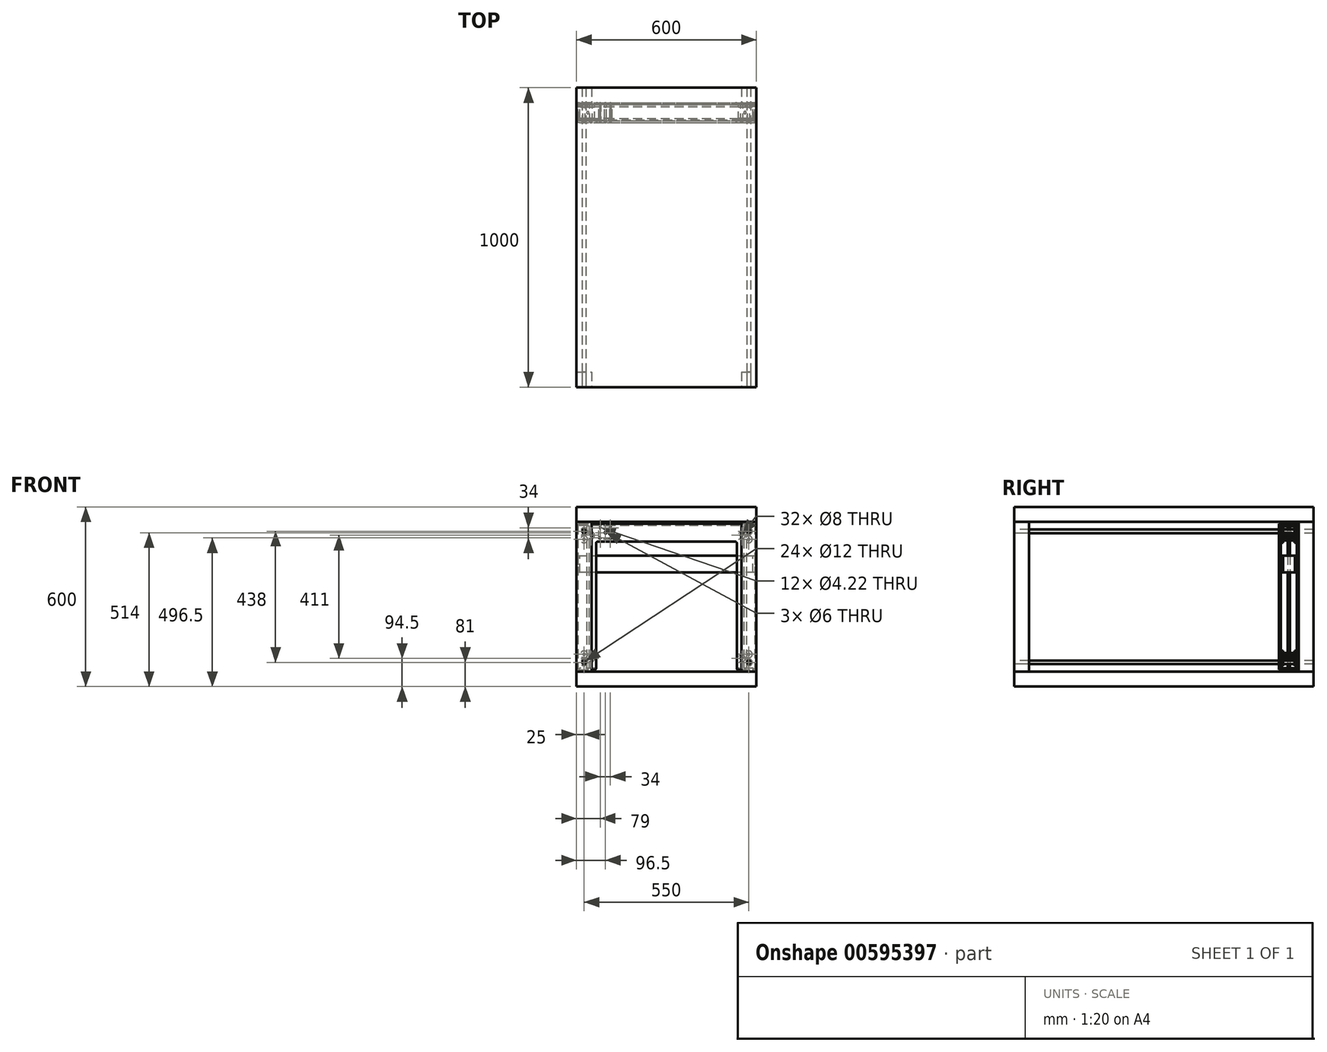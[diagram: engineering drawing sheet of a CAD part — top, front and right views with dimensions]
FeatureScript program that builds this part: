
annotation { "Feature Type Name" : "Feature", "Feature Type Description" : "" }
export const myFeature = defineFeature(function(context is Context, id is Id, definition is map)
    precondition{}
    {
        {
            var Q0;
            Q0=qCreatedBy(makeId("Front.planeOp"),FACE);
            var sketch = newSketch(context, id + "F0", { "sketchPlane" : qUnion([Q0])});
            skLineSegment(sketch, "E0.bottom", {"start": v(-300, 250) * mm, "end": v(-250, 250) * mm});
            skLineSegment(sketch, "E0.top", {"start": v(-300, -250) * mm, "end": v(-250, -250) * mm});
            skLineSegment(sketch, "E0.left", {"start": v(-300, 250) * mm, "end": v(-300, -250) * mm});
            skLineSegment(sketch, "E0.right", {"start": v(300, 250) * mm, "end": v(300, -250) * mm});
            skPoint(sketch, "E0.middle", {"position": v(0, 0) * mm});
            skLineSegment(sketch, "E1", {"start": v(-250, 250) * mm, "end": v(-250, -250) * mm});
            skLineSegment(sketch, "E2", {"start": v(-250, 250) * mm, "end": v(250, 250) * mm});
            skLineSegment(sketch, "E3", {"start": v(-250, -250) * mm, "end": v(250, -250) * mm});
            skLineSegment(sketch, "E4", {"start": v(250, -250) * mm, "end": v(250, 250) * mm});
            skLineSegment(sketch, "E5", {"start": v(250, 250) * mm, "end": v(300, 250) * mm});
            skLineSegment(sketch, "E6", {"start": v(250, -250) * mm, "end": v(300, -250) * mm});
            skLineSegment(sketch, "E7", {"start": v(-300, -250) * mm, "end": v(-300, -300) * mm});
            skLineSegment(sketch, "E8", {"start": v(-300, -300) * mm, "end": v(300, -300) * mm});
            skLineSegment(sketch, "E9", {"start": v(300, -300) * mm, "end": v(300, -250) * mm});
            skLineSegment(sketch, "E10", {"start": v(-300, 250) * mm, "end": v(-300, 300) * mm});
            skLineSegment(sketch, "E11", {"start": v(-300, 300) * mm, "end": v(300, 300) * mm});
            skLineSegment(sketch, "E12", {"start": v(300, 300) * mm, "end": v(300, 250) * mm});
            skLineSegment(sketch, "E13", {"start": v(-275, 250) * mm, "end": v(-275, 219) * mm, "construction": true});
            skLineSegment(sketch, "E14", {"start": v(275, -250) * mm, "end": v(275, 219) * mm, "construction": true});
            skCircle(sketch, "E15", {"center": v(-275, 219) * mm, "radius": 6 * mm});
            skCircle(sketch, "E16", {"center": v(275, 219) * mm, "radius": 6 * mm});
            skCircle(sketch, "E17", {"center": v(-275, -219) * mm, "radius": 6 * mm});
            skCircle(sketch, "E18", {"center": v(275, -219) * mm, "radius": 6 * mm});
            skLineSegment(sketch, "E19", {"start": v(-275, 219) * mm, "end": v(275, -219) * mm, "construction": true});
            skLineSegment(sketch, "E20", {"start": v(275, 219) * mm, "end": v(-275, -219) * mm, "construction": true});
            skLineSegment(sketch, "E21", {"start": v(275, 219) * mm, "end": v(275, 250) * mm, "construction": true});
            skLineSegment(sketch, "E22", {"start": v(-275, 219) * mm, "end": v(-275, -250) * mm, "construction": true});
            skSolve(sketch);
        }
        {
            var Q0;
            Q0=makeQuery(id+"F0.imprint","IMPRINT",FACE,{"disambiguationData":[TD([[makeQuery(id+"F0.imprint","IMPRINT",EDGE,{"derivedFrom":sQuery(id+"F0.wireOp",EDGE,"E0.bottom")}),1.0]])]});
            var Q1;
            Q1=makeQuery(id+"F0.imprint","IMPRINT",FACE,{"disambiguationData":[TD([[makeQuery(id+"F0.imprint","IMPRINT",EDGE,{"derivedFrom":sQuery(id+"F0.wireOp",EDGE,"E0.top")}),-1.0]])]});
            extrude(context, id + "F1", {"entities" : qUnion([Q0, Q1]), "oppositeDirection" : true, "depth" : 1000 * mm, "offsetDistance" : 25 * mm});
        }
        {
            var Q0;
            Q0=makeQuery(id+"F0.imprint","IMPRINT",FACE,{"disambiguationData":[TD([[makeQuery(id+"F0.imprint","IMPRINT",EDGE,{"derivedFrom":sQuery(id+"F0.wireOp",EDGE,"E0.bottom")}),-1.0]])]});
            var Q1;
            Q1=makeQuery(id+"F0.imprint","IMPRINT",FACE,{"disambiguationData":[TD([[makeQuery(id+"F0.imprint","IMPRINT",EDGE,{"derivedFrom":sQuery(id+"F0.wireOp",EDGE,"E0.right")}),-1.0]])]});
            extrude(context, id + "F2", {"entities" : qUnion([Q0, Q1]), "oppositeDirection" : true, "depth" : 50 * mm, "offsetDistance" : 25 * mm});
        }
        {
            var Q0;
            Q0=makeQuery(id+"F0.imprint","IMPRINT",FACE,{"disambiguationData":[TD([[makeQuery(id+"F0.imprint","IMPRINT",EDGE,{"derivedFrom":sQuery(id+"F0.wireOp",EDGE,"E0.bottom")}),-1.0]])]});
            var Q1;
            Q1=makeQuery(id+"F0.imprint","IMPRINT",FACE,{"disambiguationData":[TD([[makeQuery(id+"F0.imprint","IMPRINT",EDGE,{"derivedFrom":sQuery(id+"F0.wireOp",EDGE,"E0.right")}),-1.0]])]});
            var Q2;
            Q2=makeQuery(id+"F1.opExtrude","CAP_FACE",FACE,{"disambiguationData":[OSD([sQuery(id+"F0.wireOp",EDGE,"E0.bottom"),sQuery(id+"F0.wireOp",EDGE,"E2"),sQuery(id+"F0.wireOp",EDGE,"E5"),sQuery(id+"F0.wireOp",EDGE,"E10"),sQuery(id+"F0.wireOp",EDGE,"E11"),sQuery(id+"F0.wireOp",EDGE,"E12")])],"isStart":false});
            var Q3;
            Q3=makeQuery(id+"F1.opExtrude","CAP_FACE",FACE,{"disambiguationData":[OSD([sQuery(id+"F0.wireOp",EDGE,"E0.bottom"),sQuery(id+"F0.wireOp",EDGE,"E2"),sQuery(id+"F0.wireOp",EDGE,"E5"),sQuery(id+"F0.wireOp",EDGE,"E10"),sQuery(id+"F0.wireOp",EDGE,"E11"),sQuery(id+"F0.wireOp",EDGE,"E12")])],"isStart":false});
            extrude(context, id + "F3", {"entities" : qUnion([Q0, Q1]), "endBound" : BoundingType.UP_TO_SURFACE, "oppositeDirection" : true, "depth" : 1000 * mm, "endBoundEntityFace" : qUnion([Q2]), "offsetDistance" : 25 * mm, "hasSecondDirection" : true, "secondDirectionBound" : SecondDirectionBoundingType.UP_TO_SURFACE, "secondDirectionOppositeDirection" : true, "secondDirectionDepth" : 950 * mm, "secondDirectionBoundEntityFace" : qUnion([Q3]), "hasSecondDirectionOffset" : true, "secondDirectionOffsetDistance" : 50 * mm});
        }
        {
            var Q0;
            Q0=makeQuery(id+"F0.imprint","IMPRINT",FACE,{"disambiguationData":[TD([[makeQuery(id+"F0.imprint","IMPRINT",EDGE,{"derivedFrom":sQuery(id+"F0.wireOp",EDGE,"E15")}),1.0]])]});
            var Q1;
            Q1=makeQuery(id+"F0.imprint","IMPRINT",FACE,{"disambiguationData":[TD([[makeQuery(id+"F0.imprint","IMPRINT",EDGE,{"derivedFrom":sQuery(id+"F0.wireOp",EDGE,"E17")}),1.0]])]});
            var Q2;
            Q2=makeQuery(id+"F0.imprint","IMPRINT",FACE,{"disambiguationData":[TD([[makeQuery(id+"F0.imprint","IMPRINT",EDGE,{"derivedFrom":sQuery(id+"F0.wireOp",EDGE,"E18")}),1.0]])]});
            var Q3;
            Q3=makeQuery(id+"F0.imprint","IMPRINT",FACE,{"disambiguationData":[TD([[makeQuery(id+"F0.imprint","IMPRINT",EDGE,{"derivedFrom":sQuery(id+"F0.wireOp",EDGE,"E16")}),1.0]])]});
            var Q4;
            {Q4=qUnion([makeQuery(id+"F3.opExtrude","CAP_FACE",FACE,{"disambiguationData":[OSD([sQuery(id+"F0.wireOp",EDGE,"E0.bottom"),sQuery(id+"F0.wireOp",EDGE,"E0.top"),sQuery(id+"F0.wireOp",EDGE,"E0.left"),sQuery(id+"F0.wireOp",EDGE,"E1"),sQuery(id+"F0.wireOp",EDGE,"E15"),sQuery(id+"F0.wireOp",EDGE,"E17")])],"isStart":false}),makeQuery(id+"F3.opExtrude","CAP_FACE",FACE,{"disambiguationData":[OSD([sQuery(id+"F0.wireOp",EDGE,"E0.right"),sQuery(id+"F0.wireOp",EDGE,"E4"),sQuery(id+"F0.wireOp",EDGE,"E5"),sQuery(id+"F0.wireOp",EDGE,"E6"),sQuery(id+"F0.wireOp",EDGE,"E16"),sQuery(id+"F0.wireOp",EDGE,"E18")])],"isStart":false})]);}
            extrude(context, id + "F4", {"entities" : qUnion([Q0, Q1, Q2, Q3]), "endBound" : BoundingType.UP_TO_SURFACE, "oppositeDirection" : true, "depth" : 25 * mm, "endBoundEntityFace" : qUnion([Q4]), "offsetDistance" : 25 * mm});
        }
        {
            var Q0;
            Q0=makeQuery(id+"F3.opExtrude","CAP_FACE",FACE,{"disambiguationData":[OSD([sQuery(id+"F0.wireOp",EDGE,"E0.bottom"),sQuery(id+"F0.wireOp",EDGE,"E0.top"),sQuery(id+"F0.wireOp",EDGE,"E0.left"),sQuery(id+"F0.wireOp",EDGE,"E1"),sQuery(id+"F0.wireOp",EDGE,"E15"),sQuery(id+"F0.wireOp",EDGE,"E17")])],"isStart":true});
            var sketch = newSketch(context, id + "F5", { "sketchPlane" : qUnion([Q0])});
            skLineSegment(sketch, "E23.1.0", {"start": v(250, -250) * mm, "end": v(300, -250) * mm, "construction": true});
            skLineSegment(sketch, "E23.1.1", {"start": v(300, -250) * mm, "end": v(300, 250) * mm, "construction": true});
            skLineSegment(sketch, "E23.1.2", {"start": v(300, 250) * mm, "end": v(250, 250) * mm, "construction": true});
            skLineSegment(sketch, "E23.1.3", {"start": v(250, 250) * mm, "end": v(250, -250) * mm, "construction": true});
            skLineSegment(sketch, "E24.0.0", {"start": v(-300, 250) * mm, "end": v(-300, -250) * mm, "construction": true});
            skLineSegment(sketch, "E24.0.1", {"start": v(-300, -250) * mm, "end": v(-250, -250) * mm, "construction": true});
            skLineSegment(sketch, "E24.0.2", {"start": v(-250, -250) * mm, "end": v(-250, 250) * mm, "construction": true});
            skLineSegment(sketch, "E24.0.3", {"start": v(-250, 250) * mm, "end": v(-300, 250) * mm, "construction": true});
            skCircle(sketch, "E25.0", {"center": v(-275, 219) * mm, "radius": 6 * mm});
            skCircle(sketch, "E25.1", {"center": v(-275, -219) * mm, "radius": 6 * mm});
            skCircle(sketch, "E26.0", {"center": v(275, -219) * mm, "radius": 6 * mm});
            skCircle(sketch, "E26.1", {"center": v(275, 219) * mm, "radius": 6 * mm});
            skLineSegment(sketch, "E27.0.1", {"start": v(300, 250) * mm, "end": v(300, 300) * mm, "construction": true});
            skLineSegment(sketch, "E27.0.2", {"start": v(300, 300) * mm, "end": v(-300, 300) * mm, "construction": true});
            skLineSegment(sketch, "E27.0.3", {"start": v(-300, 300) * mm, "end": v(-300, 250) * mm, "construction": true});
            skLineSegment(sketch, "E28.0.1", {"start": v(-300, -250) * mm, "end": v(-300, -300) * mm, "construction": true});
            skLineSegment(sketch, "E28.0.2", {"start": v(-300, -300) * mm, "end": v(300, -300) * mm, "construction": true});
            skLineSegment(sketch, "E28.0.3", {"start": v(300, -300) * mm, "end": v(300, -250) * mm, "construction": true});
            skLineSegment(sketch, "E29", {"start": v(-250, 250) * mm, "end": v(250, 250) * mm, "construction": true});
            skLineSegment(sketch, "E30", {"start": v(-250, -250) * mm, "end": v(250, -250) * mm, "construction": true});
            skCircle(sketch, "E31", {"center": v(-275, 219) * mm, "radius": 11.5 * mm});
            skCircle(sketch, "E32", {"center": v(-275, -219) * mm, "radius": 11.5 * mm});
            skCircle(sketch, "E33", {"center": v(275, -219) * mm, "radius": 11.5 * mm});
            skCircle(sketch, "E34", {"center": v(275, 219) * mm, "radius": 11.5 * mm});
            skLineSegment(sketch, "E35.bottom", {"start": v(-290, 244) * mm, "end": v(290, 244) * mm});
            skLineSegment(sketch, "E35.top", {"start": v(-290, -244) * mm, "end": v(-240, -244) * mm});
            skLineSegment(sketch, "E35.left", {"start": v(-295, 239) * mm, "end": v(-295, -239) * mm});
            skLineSegment(sketch, "E35.right", {"start": v(295, 239) * mm, "end": v(295, -239) * mm});
            skLineSegment(sketch, "E36", {"start": v(240, -244) * mm, "end": v(290, -244) * mm});
            skLineSegment(sketch, "E37", {"start": v(-235, -239) * mm, "end": v(-235, 179) * mm});
            skLineSegment(sketch, "E38", {"start": v(-230, 184) * mm, "end": v(230, 184) * mm});
            skLineSegment(sketch, "E39", {"start": v(235, 179) * mm, "end": v(235, -239) * mm});
            skPoint(sketch, "E40.visualSharp", {"position": v(-295, 244) * mm});
            skArc(sketch, "E40.filletArc", {"start": v(-290, 244) * mm, "mid": v(-293.54, 242.54) * mm, "end": v(-295, 239) * mm});
            skPoint(sketch, "E41.visualSharp", {"position": v(-235, 184) * mm});
            skArc(sketch, "E41.filletArc", {"start": v(-230, 184) * mm, "mid": v(-233.54, 182.54) * mm, "end": v(-235, 179) * mm});
            skPoint(sketch, "E42.visualSharp", {"position": v(295, 244) * mm});
            skArc(sketch, "E42.filletArc", {"start": v(295, 239) * mm, "mid": v(293.54, 242.54) * mm, "end": v(290, 244) * mm});
            skPoint(sketch, "E43.visualSharp", {"position": v(235, 184) * mm});
            skArc(sketch, "E43.filletArc", {"start": v(235, 179) * mm, "mid": v(233.54, 182.54) * mm, "end": v(230, 184) * mm});
            skPoint(sketch, "E44.visualSharp", {"position": v(235, -244) * mm});
            skArc(sketch, "E44.filletArc", {"start": v(235, -239) * mm, "mid": v(236.46, -242.54) * mm, "end": v(240, -244) * mm});
            skPoint(sketch, "E45.visualSharp", {"position": v(295, -244) * mm});
            skArc(sketch, "E45.filletArc", {"start": v(290, -244) * mm, "mid": v(293.54, -242.54) * mm, "end": v(295, -239) * mm});
            skPoint(sketch, "E46.visualSharp", {"position": v(-295, -244) * mm});
            skArc(sketch, "E46.filletArc", {"start": v(-295, -239) * mm, "mid": v(-293.54, -242.54) * mm, "end": v(-290, -244) * mm});
            skPoint(sketch, "E47.visualSharp", {"position": v(-235, -244) * mm});
            skArc(sketch, "E47.filletArc", {"start": v(-240, -244) * mm, "mid": v(-236.46, -242.54) * mm, "end": v(-235, -239) * mm});
            skLineSegment(sketch, "E48", {"start": v(-275, 219) * mm, "end": v(275, 219) * mm, "construction": true});
            skLineSegment(sketch, "E49", {"start": v(-275, -219) * mm, "end": v(275, -219) * mm, "construction": true});
            skCircle(sketch, "E50", {"center": v(-275, -192) * mm, "radius": 4 * mm});
            skCircle(sketch, "E51", {"center": v(-251.62, -205.5) * mm, "radius": 4 * mm});
            skCircle(sketch, "E52", {"center": v(-275, 192) * mm, "radius": 4 * mm});
            skCircle(sketch, "E53", {"center": v(-251.62, 205.5) * mm, "radius": 4 * mm});
            skCircle(sketch, "E54", {"center": v(251.62, 205.5) * mm, "radius": 4 * mm});
            skCircle(sketch, "E55", {"center": v(275, 192) * mm, "radius": 4 * mm});
            skCircle(sketch, "E56", {"center": v(251.62, -205.5) * mm, "radius": 4 * mm});
            skCircle(sketch, "E57", {"center": v(275, -192) * mm, "radius": 4 * mm});
            skLineSegment(sketch, "E58", {"start": v(-275, -219) * mm, "end": v(-275, -192) * mm, "construction": true});
            skLineSegment(sketch, "E59", {"start": v(-275, -219) * mm, "end": v(-251.62, -205.5) * mm, "construction": true});
            skLineSegment(sketch, "E60", {"start": v(-275, 219) * mm, "end": v(-275, 192) * mm, "construction": true});
            skLineSegment(sketch, "E61", {"start": v(-275, 219) * mm, "end": v(-251.62, 205.5) * mm, "construction": true});
            skLineSegment(sketch, "E62", {"start": v(251.62, 205.5) * mm, "end": v(275, 219) * mm, "construction": true});
            skLineSegment(sketch, "E63", {"start": v(275, 219) * mm, "end": v(275, 192) * mm, "construction": true});
            skLineSegment(sketch, "E64", {"start": v(275, -192) * mm, "end": v(275, -219) * mm, "construction": true});
            skLineSegment(sketch, "E65", {"start": v(275, -219) * mm, "end": v(251.62, -205.5) * mm, "construction": true});
            skLineSegment(sketch, "E66", {"start": v(251.62, -205.5) * mm, "end": v(275, -192) * mm, "construction": true});
            skLineSegment(sketch, "E67", {"start": v(251.62, 205.5) * mm, "end": v(275, 192) * mm, "construction": true});
            skLineSegment(sketch, "E68", {"start": v(-275, 192) * mm, "end": v(-251.62, 205.5) * mm, "construction": true});
            skLineSegment(sketch, "E69", {"start": v(-275, -192) * mm, "end": v(-251.62, -205.5) * mm, "construction": true});
            skCircle(sketch, "E70", {"center": v(-275, 192) * mm, "radius": 11.5 * mm});
            skCircle(sketch, "E71", {"center": v(-251.62, 205.5) * mm, "radius": 11.5 * mm});
            skCircle(sketch, "E72", {"center": v(-275, -192) * mm, "radius": 11.5 * mm});
            skCircle(sketch, "E73", {"center": v(-251.62, -205.5) * mm, "radius": 11.5 * mm});
            skCircle(sketch, "E74", {"center": v(251.62, -205.5) * mm, "radius": 11.5 * mm});
            skCircle(sketch, "E75", {"center": v(275, -192) * mm, "radius": 11.5 * mm});
            skCircle(sketch, "E76", {"center": v(251.62, 205.5) * mm, "radius": 11.5 * mm});
            skCircle(sketch, "E77", {"center": v(275, 192) * mm, "radius": 11.5 * mm});
            skSolve(sketch);
        }
        {
            var Q0;
            Q0=makeQuery(id+"F5.imprint","IMPRINT",FACE,{"disambiguationData":[TD([[makeQuery(id+"F5.imprint","IMPRINT",EDGE,{"derivedFrom":sQuery(id+"F5.wireOp",EDGE,"E33")}),-1.0]])]});
            var Q1;
            Q1=makeQuery(id+"F5.imprint","IMPRINT",FACE,{"disambiguationData":[TD([[makeQuery(id+"F5.imprint","IMPRINT",EDGE,{"derivedFrom":sQuery(id+"F5.wireOp",EDGE,"E31")}),-1.0]])]});
            var Q2;
            Q2=makeQuery(id+"F5.imprint","IMPRINT",FACE,{"disambiguationData":[TD([[makeQuery(id+"F5.imprint","IMPRINT",EDGE,{"derivedFrom":sQuery(id+"F5.wireOp",EDGE,"E52")}),-1.0]])]});
            var Q3;
            {var subQ0=sQuery(id+"F5.wireOp",EDGE,"E53");var subQ1=makeQuery(id+"F3.opExtrude","CAP_EDGE",EDGE,{"disambiguationData":[OSD([sQuery(id+"F0.wireOp",EDGE,"E1")])],"isStart":true});var subQ2=makeQuery(id+"F5.imprint","INTERSECT",VERTEX,{"disambiguationData":[OD(0.0)],"derivedFrom":[subQ1,subQ0]});Q3=makeQuery(id+"F5.imprint","IMPRINT",FACE,{"disambiguationData":[TD([[makeQuery(id+"F5.imprint","IMPRINT",EDGE,{"disambiguationData":[TD([[subQ2,1.0]])],"derivedFrom":subQ0}),-1.0]])]});}
            var Q4;
            Q4=makeQuery(id+"F5.imprint","IMPRINT",FACE,{"disambiguationData":[TD([[makeQuery(id+"F5.imprint","IMPRINT",EDGE,{"derivedFrom":sQuery(id+"F5.wireOp",EDGE,"E31")}),1.0]])]});
            var Q5;
            {var subQ0=sQuery(id+"F5.wireOp",EDGE,"E53");var subQ1=makeQuery(id+"F3.opExtrude","CAP_EDGE",EDGE,{"disambiguationData":[OSD([sQuery(id+"F0.wireOp",EDGE,"E1")])],"isStart":true});var subQ2=makeQuery(id+"F5.imprint","INTERSECT",VERTEX,{"disambiguationData":[OD(0.0)],"derivedFrom":[subQ1,subQ0]});Q5=makeQuery(id+"F5.imprint","IMPRINT",FACE,{"disambiguationData":[TD([[makeQuery(id+"F5.imprint","IMPRINT",EDGE,{"disambiguationData":[TD([[subQ2,-1.0]])],"derivedFrom":subQ0}),-1.0]])]});}
            var Q6;
            Q6=makeQuery(id+"F5.imprint","IMPRINT",FACE,{"disambiguationData":[TD([[makeQuery(id+"F5.imprint","IMPRINT",EDGE,{"derivedFrom":sQuery(id+"F5.wireOp",EDGE,"E54")}),-1.0]])]});
            var Q7;
            Q7=makeQuery(id+"F5.imprint","IMPRINT",FACE,{"disambiguationData":[TD([[makeQuery(id+"F5.imprint","IMPRINT",EDGE,{"derivedFrom":sQuery(id+"F5.wireOp",EDGE,"E55")}),-1.0]])]});
            var Q8;
            Q8=makeQuery(id+"F5.imprint","IMPRINT",FACE,{"disambiguationData":[TD([[makeQuery(id+"F5.imprint","IMPRINT",EDGE,{"derivedFrom":sQuery(id+"F5.wireOp",EDGE,"E34")}),1.0]])]});
            var Q9;
            Q9=makeQuery(id+"F5.imprint","IMPRINT",FACE,{"disambiguationData":[TD([[makeQuery(id+"F5.imprint","IMPRINT",EDGE,{"derivedFrom":sQuery(id+"F5.wireOp",EDGE,"E56")}),-1.0]])]});
            var Q10;
            Q10=makeQuery(id+"F5.imprint","IMPRINT",FACE,{"disambiguationData":[TD([[makeQuery(id+"F5.imprint","IMPRINT",EDGE,{"derivedFrom":sQuery(id+"F5.wireOp",EDGE,"E57")}),-1.0]])]});
            var Q11;
            Q11=makeQuery(id+"F5.imprint","IMPRINT",FACE,{"disambiguationData":[TD([[makeQuery(id+"F5.imprint","IMPRINT",EDGE,{"derivedFrom":sQuery(id+"F5.wireOp",EDGE,"E33")}),1.0]])]});
            var Q12;
            Q12=makeQuery(id+"F5.imprint","IMPRINT",FACE,{"disambiguationData":[TD([[makeQuery(id+"F5.imprint","IMPRINT",EDGE,{"derivedFrom":sQuery(id+"F5.wireOp",EDGE,"E32")}),1.0]])]});
            var Q13;
            Q13=makeQuery(id+"F5.imprint","IMPRINT",FACE,{"disambiguationData":[TD([[makeQuery(id+"F5.imprint","IMPRINT",EDGE,{"derivedFrom":sQuery(id+"F5.wireOp",EDGE,"E50")}),-1.0]])]});
            var Q14;
            {var subQ0=sQuery(id+"F5.wireOp",EDGE,"E51");var subQ1=makeQuery(id+"F3.opExtrude","CAP_EDGE",EDGE,{"disambiguationData":[OSD([sQuery(id+"F0.wireOp",EDGE,"E1")])],"isStart":true});var subQ2=makeQuery(id+"F5.imprint","INTERSECT",VERTEX,{"disambiguationData":[OD(0.0)],"derivedFrom":[subQ1,subQ0]});Q14=makeQuery(id+"F5.imprint","IMPRINT",FACE,{"disambiguationData":[TD([[makeQuery(id+"F5.imprint","IMPRINT",EDGE,{"disambiguationData":[TD([[subQ2,1.0]])],"derivedFrom":subQ0}),-1.0]])]});}
            var Q15;
            {var subQ0=sQuery(id+"F5.wireOp",EDGE,"E51");var subQ1=makeQuery(id+"F3.opExtrude","CAP_EDGE",EDGE,{"disambiguationData":[OSD([sQuery(id+"F0.wireOp",EDGE,"E1")])],"isStart":true});var subQ2=makeQuery(id+"F5.imprint","INTERSECT",VERTEX,{"disambiguationData":[OD(0.0)],"derivedFrom":[subQ1,subQ0]});Q15=makeQuery(id+"F5.imprint","IMPRINT",FACE,{"disambiguationData":[TD([[makeQuery(id+"F5.imprint","IMPRINT",EDGE,{"disambiguationData":[TD([[subQ2,-1.0]])],"derivedFrom":subQ0}),-1.0]])]});}
            extrude(context, id + "F6", {"entities" : qUnion([Q0, Q1, Q2, Q3, Q4, Q5, Q6, Q7, Q8, Q9, Q10, Q11, Q12, Q13, Q14, Q15]), "depth" : 6 * mm, "offsetDistance" : 25 * mm});
        }
        {
            var Q0;
            Q0=makeQuery(id+"F6.opExtrude","CAP_FACE",FACE,{"disambiguationData":[OSD([sQuery(id+"F5.wireOp",EDGE,"E25.0"),sQuery(id+"F5.wireOp",EDGE,"E25.1"),sQuery(id+"F5.wireOp",EDGE,"E26.0"),sQuery(id+"F5.wireOp",EDGE,"E26.1"),sQuery(id+"F5.wireOp",EDGE,"E35.bottom"),sQuery(id+"F5.wireOp",EDGE,"E35.top"),sQuery(id+"F5.wireOp",EDGE,"E35.left"),sQuery(id+"F5.wireOp",EDGE,"E35.right"),sQuery(id+"F5.wireOp",EDGE,"E36"),sQuery(id+"F5.wireOp",EDGE,"E37"),sQuery(id+"F5.wireOp",EDGE,"E38"),sQuery(id+"F5.wireOp",EDGE,"E39"),sQuery(id+"F5.wireOp",EDGE,"E40.filletArc"),sQuery(id+"F5.wireOp",EDGE,"E41.filletArc"),sQuery(id+"F5.wireOp",EDGE,"E42.filletArc"),sQuery(id+"F5.wireOp",EDGE,"E43.filletArc"),sQuery(id+"F5.wireOp",EDGE,"E44.filletArc"),sQuery(id+"F5.wireOp",EDGE,"E45.filletArc"),sQuery(id+"F5.wireOp",EDGE,"E46.filletArc"),sQuery(id+"F5.wireOp",EDGE,"E47.filletArc"),sQuery(id+"F5.wireOp",EDGE,"E50"),sQuery(id+"F5.wireOp",EDGE,"E51"),sQuery(id+"F5.wireOp",EDGE,"E52"),sQuery(id+"F5.wireOp",EDGE,"E53"),sQuery(id+"F5.wireOp",EDGE,"E54"),sQuery(id+"F5.wireOp",EDGE,"E55"),sQuery(id+"F5.wireOp",EDGE,"E56"),sQuery(id+"F5.wireOp",EDGE,"E57")])],"isStart":false});
            extrude(context, id + "F7", {"entities" : qUnion([Q0]), "depth" : 60 * mm, "offsetDistance" : 25 * mm, "hasSecondDirection" : true, "secondDirectionOppositeDirection" : false, "secondDirectionDepth" : 54 * mm});
        }
        {
            var Q0;
            Q0=makeQuery(id+"F5.imprint","IMPRINT",FACE,{"disambiguationData":[TD([[makeQuery(id+"F5.imprint","IMPRINT",EDGE,{"derivedFrom":sQuery(id+"F5.wireOp",EDGE,"E52")}),-1.0]])]});
            var Q1;
            {var subQ0=sQuery(id+"F5.wireOp",EDGE,"E53");var subQ1=makeQuery(id+"F3.opExtrude","CAP_EDGE",EDGE,{"disambiguationData":[OSD([sQuery(id+"F0.wireOp",EDGE,"E1")])],"isStart":true});var subQ2=makeQuery(id+"F5.imprint","INTERSECT",VERTEX,{"disambiguationData":[OD(0.0)],"derivedFrom":[subQ1,subQ0]});Q1=makeQuery(id+"F5.imprint","IMPRINT",FACE,{"disambiguationData":[TD([[makeQuery(id+"F5.imprint","IMPRINT",EDGE,{"disambiguationData":[TD([[subQ2,1.0]])],"derivedFrom":subQ0}),-1.0]])]});}
            var Q2;
            {var subQ0=sQuery(id+"F5.wireOp",EDGE,"E53");var subQ1=makeQuery(id+"F3.opExtrude","CAP_EDGE",EDGE,{"disambiguationData":[OSD([sQuery(id+"F0.wireOp",EDGE,"E1")])],"isStart":true});var subQ2=makeQuery(id+"F5.imprint","INTERSECT",VERTEX,{"disambiguationData":[OD(0.0)],"derivedFrom":[subQ1,subQ0]});Q2=makeQuery(id+"F5.imprint","IMPRINT",FACE,{"disambiguationData":[TD([[makeQuery(id+"F5.imprint","IMPRINT",EDGE,{"disambiguationData":[TD([[subQ2,-1.0]])],"derivedFrom":subQ0}),-1.0]])]});}
            var Q3;
            Q3=makeQuery(id+"F5.imprint","IMPRINT",FACE,{"disambiguationData":[TD([[makeQuery(id+"F5.imprint","IMPRINT",EDGE,{"derivedFrom":sQuery(id+"F5.wireOp",EDGE,"E25.0")}),1.0]])]});
            var Q4;
            Q4=makeQuery(id+"F5.imprint","IMPRINT",FACE,{"disambiguationData":[TD([[makeQuery(id+"F5.imprint","IMPRINT",EDGE,{"derivedFrom":sQuery(id+"F5.wireOp",EDGE,"E54")}),-1.0]])]});
            var Q5;
            Q5=makeQuery(id+"F5.imprint","IMPRINT",FACE,{"disambiguationData":[TD([[makeQuery(id+"F5.imprint","IMPRINT",EDGE,{"derivedFrom":sQuery(id+"F5.wireOp",EDGE,"E26.1")}),-1.0]])]});
            var Q6;
            Q6=makeQuery(id+"F5.imprint","IMPRINT",FACE,{"disambiguationData":[TD([[makeQuery(id+"F5.imprint","IMPRINT",EDGE,{"derivedFrom":sQuery(id+"F5.wireOp",EDGE,"E55")}),-1.0]])]});
            var Q7;
            Q7=makeQuery(id+"F5.imprint","IMPRINT",FACE,{"disambiguationData":[TD([[makeQuery(id+"F5.imprint","IMPRINT",EDGE,{"derivedFrom":sQuery(id+"F5.wireOp",EDGE,"E56")}),-1.0]])]});
            var Q8;
            Q8=makeQuery(id+"F5.imprint","IMPRINT",FACE,{"disambiguationData":[TD([[makeQuery(id+"F5.imprint","IMPRINT",EDGE,{"derivedFrom":sQuery(id+"F5.wireOp",EDGE,"E57")}),-1.0]])]});
            var Q9;
            Q9=makeQuery(id+"F5.imprint","IMPRINT",FACE,{"disambiguationData":[TD([[makeQuery(id+"F5.imprint","IMPRINT",EDGE,{"derivedFrom":sQuery(id+"F5.wireOp",EDGE,"E26.0")}),-1.0]])]});
            var Q10;
            Q10=makeQuery(id+"F5.imprint","IMPRINT",FACE,{"disambiguationData":[TD([[makeQuery(id+"F5.imprint","IMPRINT",EDGE,{"derivedFrom":sQuery(id+"F5.wireOp",EDGE,"E50")}),-1.0]])]});
            var Q11;
            Q11=makeQuery(id+"F5.imprint","IMPRINT",FACE,{"disambiguationData":[TD([[makeQuery(id+"F5.imprint","IMPRINT",EDGE,{"derivedFrom":sQuery(id+"F5.wireOp",EDGE,"E25.1")}),1.0]])]});
            var Q12;
            {var subQ0=sQuery(id+"F5.wireOp",EDGE,"E51");var subQ1=makeQuery(id+"F3.opExtrude","CAP_EDGE",EDGE,{"disambiguationData":[OSD([sQuery(id+"F0.wireOp",EDGE,"E1")])],"isStart":true});var subQ2=makeQuery(id+"F5.imprint","INTERSECT",VERTEX,{"disambiguationData":[OD(0.0)],"derivedFrom":[subQ1,subQ0]});Q12=makeQuery(id+"F5.imprint","IMPRINT",FACE,{"disambiguationData":[TD([[makeQuery(id+"F5.imprint","IMPRINT",EDGE,{"disambiguationData":[TD([[subQ2,-1.0]])],"derivedFrom":subQ0}),-1.0]])]});}
            var Q13;
            {var subQ0=sQuery(id+"F5.wireOp",EDGE,"E51");var subQ1=makeQuery(id+"F3.opExtrude","CAP_EDGE",EDGE,{"disambiguationData":[OSD([sQuery(id+"F0.wireOp",EDGE,"E1")])],"isStart":true});var subQ2=makeQuery(id+"F5.imprint","INTERSECT",VERTEX,{"disambiguationData":[OD(0.0)],"derivedFrom":[subQ1,subQ0]});Q13=makeQuery(id+"F5.imprint","IMPRINT",FACE,{"disambiguationData":[TD([[makeQuery(id+"F5.imprint","IMPRINT",EDGE,{"disambiguationData":[TD([[subQ2,1.0]])],"derivedFrom":subQ0}),-1.0]])]});}
            extrude(context, id + "F8", {"entities" : qUnion([Q0, Q1, Q2, Q3, Q4, Q5, Q6, Q7, Q8, Q9, Q10, Q11, Q12, Q13]), "depth" : 14 * mm, "offsetDistance" : 25 * mm, "hasSecondDirection" : true, "secondDirectionOppositeDirection" : false, "secondDirectionDepth" : 7 * mm});
        }
        {
            var Q0;
            Q0=makeQuery(id+"F8.opExtrude","CAP_FACE",FACE,{"disambiguationData":[OSD([sQuery(id+"F5.wireOp",EDGE,"E25.1"),sQuery(id+"F5.wireOp",EDGE,"E32")])],"isStart":false});
            var Q1;
            Q1=makeQuery(id+"F8.opExtrude","CAP_FACE",FACE,{"disambiguationData":[OSD([sQuery(id+"F5.wireOp",EDGE,"E50"),sQuery(id+"F5.wireOp",EDGE,"E72")])],"isStart":false});
            var Q2;
            Q2=makeQuery(id+"F8.opExtrude","CAP_FACE",FACE,{"disambiguationData":[OSD([sQuery(id+"F5.wireOp",EDGE,"E51"),sQuery(id+"F5.wireOp",EDGE,"E73")])],"isStart":false});
            var Q3;
            Q3=makeQuery(id+"F8.opExtrude","CAP_FACE",FACE,{"disambiguationData":[OSD([sQuery(id+"F5.wireOp",EDGE,"E26.0"),sQuery(id+"F5.wireOp",EDGE,"E33")])],"isStart":false});
            var Q4;
            Q4=makeQuery(id+"F8.opExtrude","CAP_FACE",FACE,{"disambiguationData":[OSD([sQuery(id+"F5.wireOp",EDGE,"E57"),sQuery(id+"F5.wireOp",EDGE,"E75")])],"isStart":false});
            var Q5;
            Q5=makeQuery(id+"F8.opExtrude","CAP_FACE",FACE,{"disambiguationData":[OSD([sQuery(id+"F5.wireOp",EDGE,"E56"),sQuery(id+"F5.wireOp",EDGE,"E74")])],"isStart":false});
            var Q6;
            Q6=makeQuery(id+"F8.opExtrude","CAP_FACE",FACE,{"disambiguationData":[OSD([sQuery(id+"F5.wireOp",EDGE,"E26.1"),sQuery(id+"F5.wireOp",EDGE,"E34")])],"isStart":false});
            var Q7;
            Q7=makeQuery(id+"F8.opExtrude","CAP_FACE",FACE,{"disambiguationData":[OSD([sQuery(id+"F5.wireOp",EDGE,"E55"),sQuery(id+"F5.wireOp",EDGE,"E77")])],"isStart":false});
            var Q8;
            Q8=makeQuery(id+"F8.opExtrude","CAP_FACE",FACE,{"disambiguationData":[OSD([sQuery(id+"F5.wireOp",EDGE,"E54"),sQuery(id+"F5.wireOp",EDGE,"E76")])],"isStart":false});
            var Q9;
            Q9=makeQuery(id+"F8.opExtrude","CAP_FACE",FACE,{"disambiguationData":[OSD([sQuery(id+"F5.wireOp",EDGE,"E53"),sQuery(id+"F5.wireOp",EDGE,"E71")])],"isStart":false});
            var Q10;
            Q10=makeQuery(id+"F8.opExtrude","CAP_FACE",FACE,{"disambiguationData":[OSD([sQuery(id+"F5.wireOp",EDGE,"E25.0"),sQuery(id+"F5.wireOp",EDGE,"E31")])],"isStart":false});
            var Q11;
            Q11=makeQuery(id+"F8.opExtrude","CAP_FACE",FACE,{"disambiguationData":[OSD([sQuery(id+"F5.wireOp",EDGE,"E52"),sQuery(id+"F5.wireOp",EDGE,"E70")])],"isStart":false});
            var Q12;
            Q12=makeQuery(id+"F7.opExtrude","CAP_FACE",FACE,{"disambiguationData":[OSD([sQuery(id+"F5.wireOp",EDGE,"E25.0"),sQuery(id+"F5.wireOp",EDGE,"E25.1"),sQuery(id+"F5.wireOp",EDGE,"E26.0"),sQuery(id+"F5.wireOp",EDGE,"E26.1"),sQuery(id+"F5.wireOp",EDGE,"E35.bottom"),sQuery(id+"F5.wireOp",EDGE,"E35.top"),sQuery(id+"F5.wireOp",EDGE,"E35.left"),sQuery(id+"F5.wireOp",EDGE,"E35.right"),sQuery(id+"F5.wireOp",EDGE,"E36"),sQuery(id+"F5.wireOp",EDGE,"E37"),sQuery(id+"F5.wireOp",EDGE,"E38"),sQuery(id+"F5.wireOp",EDGE,"E39"),sQuery(id+"F5.wireOp",EDGE,"E40.filletArc"),sQuery(id+"F5.wireOp",EDGE,"E41.filletArc"),sQuery(id+"F5.wireOp",EDGE,"E42.filletArc"),sQuery(id+"F5.wireOp",EDGE,"E43.filletArc"),sQuery(id+"F5.wireOp",EDGE,"E44.filletArc"),sQuery(id+"F5.wireOp",EDGE,"E45.filletArc"),sQuery(id+"F5.wireOp",EDGE,"E46.filletArc"),sQuery(id+"F5.wireOp",EDGE,"E47.filletArc"),sQuery(id+"F5.wireOp",EDGE,"E50"),sQuery(id+"F5.wireOp",EDGE,"E51"),sQuery(id+"F5.wireOp",EDGE,"E52"),sQuery(id+"F5.wireOp",EDGE,"E53"),sQuery(id+"F5.wireOp",EDGE,"E54"),sQuery(id+"F5.wireOp",EDGE,"E55"),sQuery(id+"F5.wireOp",EDGE,"E56"),sQuery(id+"F5.wireOp",EDGE,"E57")])],"isStart":true});
            var Q13;
            Q13=makeQuery(id+"F7.opExtrude","CAP_FACE",FACE,{"disambiguationData":[OSD([sQuery(id+"F5.wireOp",EDGE,"E25.0"),sQuery(id+"F5.wireOp",EDGE,"E25.1"),sQuery(id+"F5.wireOp",EDGE,"E26.0"),sQuery(id+"F5.wireOp",EDGE,"E26.1"),sQuery(id+"F5.wireOp",EDGE,"E35.bottom"),sQuery(id+"F5.wireOp",EDGE,"E35.top"),sQuery(id+"F5.wireOp",EDGE,"E35.left"),sQuery(id+"F5.wireOp",EDGE,"E35.right"),sQuery(id+"F5.wireOp",EDGE,"E36"),sQuery(id+"F5.wireOp",EDGE,"E37"),sQuery(id+"F5.wireOp",EDGE,"E38"),sQuery(id+"F5.wireOp",EDGE,"E39"),sQuery(id+"F5.wireOp",EDGE,"E40.filletArc"),sQuery(id+"F5.wireOp",EDGE,"E41.filletArc"),sQuery(id+"F5.wireOp",EDGE,"E42.filletArc"),sQuery(id+"F5.wireOp",EDGE,"E43.filletArc"),sQuery(id+"F5.wireOp",EDGE,"E44.filletArc"),sQuery(id+"F5.wireOp",EDGE,"E45.filletArc"),sQuery(id+"F5.wireOp",EDGE,"E46.filletArc"),sQuery(id+"F5.wireOp",EDGE,"E47.filletArc"),sQuery(id+"F5.wireOp",EDGE,"E50"),sQuery(id+"F5.wireOp",EDGE,"E51"),sQuery(id+"F5.wireOp",EDGE,"E52"),sQuery(id+"F5.wireOp",EDGE,"E53"),sQuery(id+"F5.wireOp",EDGE,"E54"),sQuery(id+"F5.wireOp",EDGE,"E55"),sQuery(id+"F5.wireOp",EDGE,"E56"),sQuery(id+"F5.wireOp",EDGE,"E57")])],"isStart":true});
            extrude(context, id + "F9", {"entities" : qUnion([Q0, Q1, Q2, Q3, Q4, Q5, Q6, Q7, Q8, Q9, Q10, Q11]), "endBound" : BoundingType.UP_TO_SURFACE, "depth" : 25 * mm, "endBoundEntityFace" : qUnion([Q12]), "hasOffset" : true, "offsetDistance" : 1 * mm, "hasSecondDirection" : true, "secondDirectionBound" : SecondDirectionBoundingType.UP_TO_SURFACE, "secondDirectionOppositeDirection" : false, "secondDirectionDepth" : 25 * mm, "secondDirectionBoundEntityFace" : qUnion([Q13]), "hasSecondDirectionOffset" : true, "secondDirectionOffsetDistance" : 8 * mm});
        }
        {
            var Q0;
            Q0=makeQuery(id+"F5.imprint","IMPRINT",FACE,{"disambiguationData":[TD([[makeQuery(id+"F5.imprint","IMPRINT",EDGE,{"derivedFrom":sQuery(id+"F5.wireOp",EDGE,"E52")}),1.0]])]});
            var Q1;
            {var subQ0=sQuery(id+"F5.wireOp",EDGE,"E53");var subQ1=makeQuery(id+"F3.opExtrude","CAP_EDGE",EDGE,{"disambiguationData":[OSD([sQuery(id+"F0.wireOp",EDGE,"E1")])],"isStart":true});var subQ2=makeQuery(id+"F5.imprint","INTERSECT",VERTEX,{"disambiguationData":[OD(0.0)],"derivedFrom":[subQ1,subQ0]});Q1=makeQuery(id+"F5.imprint","IMPRINT",FACE,{"disambiguationData":[TD([[makeQuery(id+"F5.imprint","IMPRINT",EDGE,{"disambiguationData":[TD([[subQ2,1.0]])],"derivedFrom":subQ0}),1.0]])]});}
            var Q2;
            {var subQ0=sQuery(id+"F5.wireOp",EDGE,"E53");var subQ1=makeQuery(id+"F3.opExtrude","CAP_EDGE",EDGE,{"disambiguationData":[OSD([sQuery(id+"F0.wireOp",EDGE,"E1")])],"isStart":true});var subQ2=makeQuery(id+"F5.imprint","INTERSECT",VERTEX,{"disambiguationData":[OD(0.0)],"derivedFrom":[subQ1,subQ0]});Q2=makeQuery(id+"F5.imprint","IMPRINT",FACE,{"disambiguationData":[TD([[makeQuery(id+"F5.imprint","IMPRINT",EDGE,{"disambiguationData":[TD([[subQ2,-1.0]])],"derivedFrom":subQ0}),1.0]])]});}
            var Q3;
            Q3=makeQuery(id+"F5.imprint","IMPRINT",FACE,{"disambiguationData":[TD([[makeQuery(id+"F5.imprint","IMPRINT",EDGE,{"derivedFrom":sQuery(id+"F5.wireOp",EDGE,"E50")}),1.0]])]});
            var Q4;
            {var subQ0=sQuery(id+"F5.wireOp",EDGE,"E51");var subQ1=makeQuery(id+"F3.opExtrude","CAP_EDGE",EDGE,{"disambiguationData":[OSD([sQuery(id+"F0.wireOp",EDGE,"E1")])],"isStart":true});var subQ2=makeQuery(id+"F5.imprint","INTERSECT",VERTEX,{"disambiguationData":[OD(0.0)],"derivedFrom":[subQ1,subQ0]});Q4=makeQuery(id+"F5.imprint","IMPRINT",FACE,{"disambiguationData":[TD([[makeQuery(id+"F5.imprint","IMPRINT",EDGE,{"disambiguationData":[TD([[subQ2,-1.0]])],"derivedFrom":subQ0}),1.0]])]});}
            var Q5;
            {var subQ0=sQuery(id+"F5.wireOp",EDGE,"E51");var subQ1=makeQuery(id+"F3.opExtrude","CAP_EDGE",EDGE,{"disambiguationData":[OSD([sQuery(id+"F0.wireOp",EDGE,"E1")])],"isStart":true});var subQ2=makeQuery(id+"F5.imprint","INTERSECT",VERTEX,{"disambiguationData":[OD(0.0)],"derivedFrom":[subQ1,subQ0]});Q5=makeQuery(id+"F5.imprint","IMPRINT",FACE,{"disambiguationData":[TD([[makeQuery(id+"F5.imprint","IMPRINT",EDGE,{"disambiguationData":[TD([[subQ2,1.0]])],"derivedFrom":subQ0}),1.0]])]});}
            var Q6;
            Q6=makeQuery(id+"F5.imprint","IMPRINT",FACE,{"disambiguationData":[TD([[makeQuery(id+"F5.imprint","IMPRINT",EDGE,{"derivedFrom":sQuery(id+"F5.wireOp",EDGE,"E54")}),1.0]])]});
            var Q7;
            Q7=makeQuery(id+"F5.imprint","IMPRINT",FACE,{"disambiguationData":[TD([[makeQuery(id+"F5.imprint","IMPRINT",EDGE,{"derivedFrom":sQuery(id+"F5.wireOp",EDGE,"E55")}),1.0]])]});
            var Q8;
            Q8=makeQuery(id+"F5.imprint","IMPRINT",FACE,{"disambiguationData":[TD([[makeQuery(id+"F5.imprint","IMPRINT",EDGE,{"derivedFrom":sQuery(id+"F5.wireOp",EDGE,"E56")}),1.0]])]});
            var Q9;
            Q9=makeQuery(id+"F5.imprint","IMPRINT",FACE,{"disambiguationData":[TD([[makeQuery(id+"F5.imprint","IMPRINT",EDGE,{"derivedFrom":sQuery(id+"F5.wireOp",EDGE,"E57")}),1.0]])]});
            var Q10;
            Q10=makeQuery(id+"F7.opExtrude","CAP_FACE",FACE,{"disambiguationData":[OSD([sQuery(id+"F5.wireOp",EDGE,"E25.0"),sQuery(id+"F5.wireOp",EDGE,"E25.1"),sQuery(id+"F5.wireOp",EDGE,"E26.0"),sQuery(id+"F5.wireOp",EDGE,"E26.1"),sQuery(id+"F5.wireOp",EDGE,"E35.bottom"),sQuery(id+"F5.wireOp",EDGE,"E35.top"),sQuery(id+"F5.wireOp",EDGE,"E35.left"),sQuery(id+"F5.wireOp",EDGE,"E35.right"),sQuery(id+"F5.wireOp",EDGE,"E36"),sQuery(id+"F5.wireOp",EDGE,"E37"),sQuery(id+"F5.wireOp",EDGE,"E38"),sQuery(id+"F5.wireOp",EDGE,"E39"),sQuery(id+"F5.wireOp",EDGE,"E40.filletArc"),sQuery(id+"F5.wireOp",EDGE,"E41.filletArc"),sQuery(id+"F5.wireOp",EDGE,"E42.filletArc"),sQuery(id+"F5.wireOp",EDGE,"E43.filletArc"),sQuery(id+"F5.wireOp",EDGE,"E44.filletArc"),sQuery(id+"F5.wireOp",EDGE,"E45.filletArc"),sQuery(id+"F5.wireOp",EDGE,"E46.filletArc"),sQuery(id+"F5.wireOp",EDGE,"E47.filletArc"),sQuery(id+"F5.wireOp",EDGE,"E50"),sQuery(id+"F5.wireOp",EDGE,"E51"),sQuery(id+"F5.wireOp",EDGE,"E52"),sQuery(id+"F5.wireOp",EDGE,"E53"),sQuery(id+"F5.wireOp",EDGE,"E54"),sQuery(id+"F5.wireOp",EDGE,"E55"),sQuery(id+"F5.wireOp",EDGE,"E56"),sQuery(id+"F5.wireOp",EDGE,"E57")])],"isStart":false});
            extrude(context, id + "F10", {"entities" : qUnion([Q0, Q1, Q2, Q3, Q4, Q5, Q6, Q7, Q8, Q9]), "endBound" : BoundingType.UP_TO_SURFACE, "depth" : 25 * mm, "endBoundEntityFace" : qUnion([Q10]), "offsetDistance" : 25 * mm});
        }
        {
            var Q0;
            Q0=makeQuery(id+"F6.opExtrude","CAP_FACE",FACE,{"disambiguationData":[OSD([sQuery(id+"F5.wireOp",EDGE,"E25.0"),sQuery(id+"F5.wireOp",EDGE,"E25.1"),sQuery(id+"F5.wireOp",EDGE,"E26.0"),sQuery(id+"F5.wireOp",EDGE,"E26.1"),sQuery(id+"F5.wireOp",EDGE,"E35.bottom"),sQuery(id+"F5.wireOp",EDGE,"E35.top"),sQuery(id+"F5.wireOp",EDGE,"E35.left"),sQuery(id+"F5.wireOp",EDGE,"E35.right"),sQuery(id+"F5.wireOp",EDGE,"E36"),sQuery(id+"F5.wireOp",EDGE,"E37"),sQuery(id+"F5.wireOp",EDGE,"E38"),sQuery(id+"F5.wireOp",EDGE,"E39"),sQuery(id+"F5.wireOp",EDGE,"E40.filletArc"),sQuery(id+"F5.wireOp",EDGE,"E41.filletArc"),sQuery(id+"F5.wireOp",EDGE,"E42.filletArc"),sQuery(id+"F5.wireOp",EDGE,"E43.filletArc"),sQuery(id+"F5.wireOp",EDGE,"E44.filletArc"),sQuery(id+"F5.wireOp",EDGE,"E45.filletArc"),sQuery(id+"F5.wireOp",EDGE,"E46.filletArc"),sQuery(id+"F5.wireOp",EDGE,"E47.filletArc"),sQuery(id+"F5.wireOp",EDGE,"E50"),sQuery(id+"F5.wireOp",EDGE,"E51"),sQuery(id+"F5.wireOp",EDGE,"E52"),sQuery(id+"F5.wireOp",EDGE,"E53"),sQuery(id+"F5.wireOp",EDGE,"E54"),sQuery(id+"F5.wireOp",EDGE,"E55"),sQuery(id+"F5.wireOp",EDGE,"E56"),sQuery(id+"F5.wireOp",EDGE,"E57")])],"isStart":false});
            var sketch = newSketch(context, id + "F11", { "sketchPlane" : qUnion([Q0])});
            skLineSegment(sketch, "E78.bottom", {"start": v(-181, 191.5) * mm, "end": v(-226, 191.5) * mm});
            skLineSegment(sketch, "E78.top", {"start": v(-181, 236.5) * mm, "end": v(-226, 236.5) * mm});
            skLineSegment(sketch, "E78.left", {"start": v(-181, 191.5) * mm, "end": v(-181, 236.5) * mm});
            skLineSegment(sketch, "E78.right", {"start": v(-226, 191.5) * mm, "end": v(-226, 236.5) * mm});
            skPoint(sketch, "E78.middle", {"position": v(-203.5, 214) * mm});
            skLineSegment(sketch, "E79", {"start": v(-203.5, 191.5) * mm, "end": v(-203.5, 184) * mm, "construction": true});
            skLineSegment(sketch, "E80", {"start": v(-203.5, 236.5) * mm, "end": v(-203.5, 244) * mm, "construction": true});
            skCircle(sketch, "E81", {"center": v(-187, 196.5) * mm, "radius": 2.11 * mm});
            skCircle(sketch, "E82", {"center": v(-221, 230.5) * mm, "radius": 2.11 * mm});
            skLineSegment(sketch, "E83.bottom", {"start": v(-221, 230.5) * mm, "end": v(-187, 230.5) * mm, "construction": true});
            skLineSegment(sketch, "E83.top", {"start": v(-221, 196.5) * mm, "end": v(-187, 196.5) * mm, "construction": true});
            skLineSegment(sketch, "E83.left", {"start": v(-221, 230.5) * mm, "end": v(-221, 196.5) * mm, "construction": true});
            skLineSegment(sketch, "E83.right", {"start": v(-187, 230.5) * mm, "end": v(-187, 196.5) * mm, "construction": true});
            skCircle(sketch, "E84", {"center": v(-187, 230.5) * mm, "radius": 2.11 * mm});
            skCircle(sketch, "E85", {"center": v(-221, 196.5) * mm, "radius": 2.11 * mm});
            skCircle(sketch, "E86", {"center": v(-203.5, 214) * mm, "radius": 3 * mm});
            skLineSegment(sketch, "E87.0.0", {"start": v(290, 244) * mm, "end": v(-290, 244) * mm});
            skArc(sketch, "E87.0.1", {"start": v(-290, 244) * mm, "mid": v(-293.54, 242.54) * mm, "end": v(-295, 239) * mm});
            skLineSegment(sketch, "E87.0.2", {"start": v(-295, 239) * mm, "end": v(-295, -239) * mm});
            skArc(sketch, "E87.0.3", {"start": v(-295, -239) * mm, "mid": v(-293.54, -242.54) * mm, "end": v(-290, -244) * mm});
            skLineSegment(sketch, "E87.0.4", {"start": v(-290, -244) * mm, "end": v(-240, -244) * mm});
            skArc(sketch, "E87.0.5", {"start": v(-240, -244) * mm, "mid": v(-236.46, -242.54) * mm, "end": v(-235, -239) * mm});
            skLineSegment(sketch, "E87.0.6", {"start": v(-235, -239) * mm, "end": v(-235, 179) * mm});
            skArc(sketch, "E87.0.7", {"start": v(-235, 179) * mm, "mid": v(-233.54, 182.54) * mm, "end": v(-230, 184) * mm});
            skLineSegment(sketch, "E87.0.8", {"start": v(-230, 184) * mm, "end": v(230, 184) * mm});
            skArc(sketch, "E87.0.9", {"start": v(230, 184) * mm, "mid": v(233.54, 182.54) * mm, "end": v(235, 179) * mm});
            skLineSegment(sketch, "E87.0.10", {"start": v(235, 179) * mm, "end": v(235, -239) * mm});
            skArc(sketch, "E87.0.11", {"start": v(235, -239) * mm, "mid": v(236.46, -242.54) * mm, "end": v(240, -244) * mm});
            skLineSegment(sketch, "E87.0.12", {"start": v(240, -244) * mm, "end": v(290, -244) * mm});
            skArc(sketch, "E87.0.13", {"start": v(290, -244) * mm, "mid": v(293.54, -242.54) * mm, "end": v(295, -239) * mm});
            skLineSegment(sketch, "E87.0.14", {"start": v(295, -239) * mm, "end": v(295, 239) * mm});
            skArc(sketch, "E87.0.15", {"start": v(295, 239) * mm, "mid": v(293.54, 242.54) * mm, "end": v(290, 244) * mm});
            skLineSegment(sketch, "E88", {"start": v(-290, 244) * mm, "end": v(-290, 238) * mm});
            skLineSegment(sketch, "E89", {"start": v(290, 244) * mm, "end": v(290, 238) * mm});
            skLineSegment(sketch, "E90", {"start": v(290, 238) * mm, "end": v(-290, 238) * mm});
            skLineSegment(sketch, "E91", {"start": v(-290, -244) * mm, "end": v(-290, -238) * mm});
            skLineSegment(sketch, "E92", {"start": v(-240, -244) * mm, "end": v(-240, -238) * mm});
            skLineSegment(sketch, "E93", {"start": v(-240, -238) * mm, "end": v(-290, -238) * mm});
            skLineSegment(sketch, "E94", {"start": v(240, -244) * mm, "end": v(240, -238) * mm});
            skLineSegment(sketch, "E95", {"start": v(290, -244) * mm, "end": v(290, -238) * mm});
            skLineSegment(sketch, "E96", {"start": v(290, -238) * mm, "end": v(240, -238) * mm});
            skSolve(sketch);
        }
        {
            var Q0;
            Q0=makeQuery(id+"F11.imprint","IMPRINT",FACE,{"disambiguationData":[TD([[makeQuery(id+"F11.imprint","IMPRINT",EDGE,{"derivedFrom":sQuery(id+"F11.wireOp",EDGE,"E78.bottom")}),-1.0]])]});
            var Q1;
            Q1=makeQuery(id+"F9.opExtrude","CAP_FACE",FACE,{"disambiguationData":[OSD([sQuery(id+"F5.wireOp",EDGE,"E53"),sQuery(id+"F5.wireOp",EDGE,"E71")])],"isStart":true});
            var Q2;
            Q2=makeQuery(id+"F8.opExtrude","CAP_FACE",FACE,{"disambiguationData":[OSD([sQuery(id+"F5.wireOp",EDGE,"E52"),sQuery(id+"F5.wireOp",EDGE,"E70")])],"isStart":false});
            extrude(context, id + "F12", {"entities" : qUnion([Q0]), "endBound" : BoundingType.UP_TO_SURFACE, "depth" : 25 * mm, "endBoundEntityFace" : qUnion([Q1]), "offsetDistance" : 25 * mm, "hasSecondDirection" : true, "secondDirectionBound" : SecondDirectionBoundingType.UP_TO_SURFACE, "secondDirectionOppositeDirection" : false, "secondDirectionDepth" : 25 * mm, "secondDirectionBoundEntityFace" : qUnion([Q2])});
        }
        {
            var Q0;
            Q0=makeQuery(id+"F11.imprint","IMPRINT",FACE,{"disambiguationData":[TD([[makeQuery(id+"F11.imprint","IMPRINT",EDGE,{"derivedFrom":sQuery(id+"F11.wireOp",EDGE,"E86")}),1.0]])]});
            var Q1;
            Q1=makeQuery(id+"F11.imprint","IMPRINT",FACE,{"disambiguationData":[TD([[makeQuery(id+"F11.imprint","IMPRINT",EDGE,{"derivedFrom":sQuery(id+"F11.wireOp",EDGE,"E85")}),1.0]])]});
            var Q2;
            Q2=makeQuery(id+"F11.imprint","IMPRINT",FACE,{"disambiguationData":[TD([[makeQuery(id+"F11.imprint","IMPRINT",EDGE,{"derivedFrom":sQuery(id+"F11.wireOp",EDGE,"E81")}),1.0]])]});
            var Q3;
            Q3=makeQuery(id+"F11.imprint","IMPRINT",FACE,{"disambiguationData":[TD([[makeQuery(id+"F11.imprint","IMPRINT",EDGE,{"derivedFrom":sQuery(id+"F11.wireOp",EDGE,"E82")}),1.0]])]});
            var Q4;
            Q4=makeQuery(id+"F11.imprint","IMPRINT",FACE,{"disambiguationData":[TD([[makeQuery(id+"F11.imprint","IMPRINT",EDGE,{"derivedFrom":sQuery(id+"F11.wireOp",EDGE,"E84")}),1.0]])]});
            var Q5;
            Q5=makeQuery(id+"F7.opExtrude","CAP_FACE",FACE,{"disambiguationData":[OSD([sQuery(id+"F5.wireOp",EDGE,"E25.0"),sQuery(id+"F5.wireOp",EDGE,"E25.1"),sQuery(id+"F5.wireOp",EDGE,"E26.0"),sQuery(id+"F5.wireOp",EDGE,"E26.1"),sQuery(id+"F5.wireOp",EDGE,"E35.bottom"),sQuery(id+"F5.wireOp",EDGE,"E35.top"),sQuery(id+"F5.wireOp",EDGE,"E35.left"),sQuery(id+"F5.wireOp",EDGE,"E35.right"),sQuery(id+"F5.wireOp",EDGE,"E36"),sQuery(id+"F5.wireOp",EDGE,"E37"),sQuery(id+"F5.wireOp",EDGE,"E38"),sQuery(id+"F5.wireOp",EDGE,"E39"),sQuery(id+"F5.wireOp",EDGE,"E40.filletArc"),sQuery(id+"F5.wireOp",EDGE,"E41.filletArc"),sQuery(id+"F5.wireOp",EDGE,"E42.filletArc"),sQuery(id+"F5.wireOp",EDGE,"E43.filletArc"),sQuery(id+"F5.wireOp",EDGE,"E44.filletArc"),sQuery(id+"F5.wireOp",EDGE,"E45.filletArc"),sQuery(id+"F5.wireOp",EDGE,"E46.filletArc"),sQuery(id+"F5.wireOp",EDGE,"E47.filletArc"),sQuery(id+"F5.wireOp",EDGE,"E50"),sQuery(id+"F5.wireOp",EDGE,"E51"),sQuery(id+"F5.wireOp",EDGE,"E52"),sQuery(id+"F5.wireOp",EDGE,"E53"),sQuery(id+"F5.wireOp",EDGE,"E54"),sQuery(id+"F5.wireOp",EDGE,"E55"),sQuery(id+"F5.wireOp",EDGE,"E56"),sQuery(id+"F5.wireOp",EDGE,"E57")])],"isStart":false});
            var Q6;
            Q6=makeQuery(id+"F6.opExtrude","CAP_FACE",FACE,{"disambiguationData":[OSD([sQuery(id+"F5.wireOp",EDGE,"E25.0"),sQuery(id+"F5.wireOp",EDGE,"E25.1"),sQuery(id+"F5.wireOp",EDGE,"E26.0"),sQuery(id+"F5.wireOp",EDGE,"E26.1"),sQuery(id+"F5.wireOp",EDGE,"E35.bottom"),sQuery(id+"F5.wireOp",EDGE,"E35.top"),sQuery(id+"F5.wireOp",EDGE,"E35.left"),sQuery(id+"F5.wireOp",EDGE,"E35.right"),sQuery(id+"F5.wireOp",EDGE,"E36"),sQuery(id+"F5.wireOp",EDGE,"E37"),sQuery(id+"F5.wireOp",EDGE,"E38"),sQuery(id+"F5.wireOp",EDGE,"E39"),sQuery(id+"F5.wireOp",EDGE,"E40.filletArc"),sQuery(id+"F5.wireOp",EDGE,"E41.filletArc"),sQuery(id+"F5.wireOp",EDGE,"E42.filletArc"),sQuery(id+"F5.wireOp",EDGE,"E43.filletArc"),sQuery(id+"F5.wireOp",EDGE,"E44.filletArc"),sQuery(id+"F5.wireOp",EDGE,"E45.filletArc"),sQuery(id+"F5.wireOp",EDGE,"E46.filletArc"),sQuery(id+"F5.wireOp",EDGE,"E47.filletArc"),sQuery(id+"F5.wireOp",EDGE,"E50"),sQuery(id+"F5.wireOp",EDGE,"E51"),sQuery(id+"F5.wireOp",EDGE,"E52"),sQuery(id+"F5.wireOp",EDGE,"E53"),sQuery(id+"F5.wireOp",EDGE,"E54"),sQuery(id+"F5.wireOp",EDGE,"E55"),sQuery(id+"F5.wireOp",EDGE,"E56"),sQuery(id+"F5.wireOp",EDGE,"E57")])],"isStart":true});
            extrude(context, id + "F13", {"entities" : qUnion([Q0, Q1, Q2, Q3, Q4]), "operationType" : NewBodyOperationType.REMOVE, "endBound" : BoundingType.UP_TO_SURFACE, "depth" : 25 * mm, "endBoundEntityFace" : qUnion([Q5]), "offsetDistance" : 25 * mm, "hasSecondDirection" : true, "secondDirectionBound" : SecondDirectionBoundingType.UP_TO_SURFACE, "secondDirectionOppositeDirection" : true, "secondDirectionDepth" : 25 * mm, "secondDirectionBoundEntityFace" : qUnion([Q6])});
        }
        {
            var Q0;
            Q0=makeQuery(id+"F11.imprint","IMPRINT",FACE,{"disambiguationData":[TD([[makeQuery(id+"F11.imprint","IMPRINT",EDGE,{"derivedFrom":sQuery(id+"F11.wireOp",EDGE,"E86")}),1.0]])]});
            var Q1;
            Q1=makeQuery(id+"F7.opExtrude","CAP_FACE",FACE,{"disambiguationData":[OSD([sQuery(id+"F5.wireOp",EDGE,"E25.0"),sQuery(id+"F5.wireOp",EDGE,"E25.1"),sQuery(id+"F5.wireOp",EDGE,"E26.0"),sQuery(id+"F5.wireOp",EDGE,"E26.1"),sQuery(id+"F5.wireOp",EDGE,"E35.bottom"),sQuery(id+"F5.wireOp",EDGE,"E35.top"),sQuery(id+"F5.wireOp",EDGE,"E35.left"),sQuery(id+"F5.wireOp",EDGE,"E35.right"),sQuery(id+"F5.wireOp",EDGE,"E36"),sQuery(id+"F5.wireOp",EDGE,"E37"),sQuery(id+"F5.wireOp",EDGE,"E38"),sQuery(id+"F5.wireOp",EDGE,"E39"),sQuery(id+"F5.wireOp",EDGE,"E40.filletArc"),sQuery(id+"F5.wireOp",EDGE,"E41.filletArc"),sQuery(id+"F5.wireOp",EDGE,"E42.filletArc"),sQuery(id+"F5.wireOp",EDGE,"E43.filletArc"),sQuery(id+"F5.wireOp",EDGE,"E44.filletArc"),sQuery(id+"F5.wireOp",EDGE,"E45.filletArc"),sQuery(id+"F5.wireOp",EDGE,"E46.filletArc"),sQuery(id+"F5.wireOp",EDGE,"E47.filletArc"),sQuery(id+"F5.wireOp",EDGE,"E50"),sQuery(id+"F5.wireOp",EDGE,"E51"),sQuery(id+"F5.wireOp",EDGE,"E52"),sQuery(id+"F5.wireOp",EDGE,"E53"),sQuery(id+"F5.wireOp",EDGE,"E54"),sQuery(id+"F5.wireOp",EDGE,"E55"),sQuery(id+"F5.wireOp",EDGE,"E56"),sQuery(id+"F5.wireOp",EDGE,"E57")])],"isStart":true});
            extrude(context, id + "F14", {"entities" : qUnion([Q0]), "endBound" : BoundingType.UP_TO_SURFACE, "depth" : 25 * mm, "endBoundEntityFace" : qUnion([Q1]), "offsetDistance" : 25 * mm});
        }
        {
            var Q0;
            Q0=makeQuery(id+"F11.imprint","IMPRINT",FACE,{"disambiguationData":[TD([[makeQuery(id+"F11.imprint","IMPRINT",EDGE,{"derivedFrom":sQuery(id+"F11.wireOp",EDGE,"E85")}),1.0]])]});
            var Q1;
            Q1=makeQuery(id+"F11.imprint","IMPRINT",FACE,{"disambiguationData":[TD([[makeQuery(id+"F11.imprint","IMPRINT",EDGE,{"derivedFrom":sQuery(id+"F11.wireOp",EDGE,"E81")}),1.0]])]});
            var Q2;
            Q2=makeQuery(id+"F11.imprint","IMPRINT",FACE,{"disambiguationData":[TD([[makeQuery(id+"F11.imprint","IMPRINT",EDGE,{"derivedFrom":sQuery(id+"F11.wireOp",EDGE,"E82")}),1.0]])]});
            var Q3;
            Q3=makeQuery(id+"F11.imprint","IMPRINT",FACE,{"disambiguationData":[TD([[makeQuery(id+"F11.imprint","IMPRINT",EDGE,{"derivedFrom":sQuery(id+"F11.wireOp",EDGE,"E84")}),1.0]])]});
            var Q4;
            Q4=makeQuery(id+"F6.opExtrude","CAP_FACE",FACE,{"disambiguationData":[OSD([sQuery(id+"F5.wireOp",EDGE,"E25.0"),sQuery(id+"F5.wireOp",EDGE,"E25.1"),sQuery(id+"F5.wireOp",EDGE,"E26.0"),sQuery(id+"F5.wireOp",EDGE,"E26.1"),sQuery(id+"F5.wireOp",EDGE,"E35.bottom"),sQuery(id+"F5.wireOp",EDGE,"E35.top"),sQuery(id+"F5.wireOp",EDGE,"E35.left"),sQuery(id+"F5.wireOp",EDGE,"E35.right"),sQuery(id+"F5.wireOp",EDGE,"E36"),sQuery(id+"F5.wireOp",EDGE,"E37"),sQuery(id+"F5.wireOp",EDGE,"E38"),sQuery(id+"F5.wireOp",EDGE,"E39"),sQuery(id+"F5.wireOp",EDGE,"E40.filletArc"),sQuery(id+"F5.wireOp",EDGE,"E41.filletArc"),sQuery(id+"F5.wireOp",EDGE,"E42.filletArc"),sQuery(id+"F5.wireOp",EDGE,"E43.filletArc"),sQuery(id+"F5.wireOp",EDGE,"E44.filletArc"),sQuery(id+"F5.wireOp",EDGE,"E45.filletArc"),sQuery(id+"F5.wireOp",EDGE,"E46.filletArc"),sQuery(id+"F5.wireOp",EDGE,"E47.filletArc"),sQuery(id+"F5.wireOp",EDGE,"E50"),sQuery(id+"F5.wireOp",EDGE,"E51"),sQuery(id+"F5.wireOp",EDGE,"E52"),sQuery(id+"F5.wireOp",EDGE,"E53"),sQuery(id+"F5.wireOp",EDGE,"E54"),sQuery(id+"F5.wireOp",EDGE,"E55"),sQuery(id+"F5.wireOp",EDGE,"E56"),sQuery(id+"F5.wireOp",EDGE,"E57")])],"isStart":true});
            var Q5;
            Q5=makeQuery(id+"F7.opExtrude","CAP_FACE",FACE,{"disambiguationData":[OSD([sQuery(id+"F5.wireOp",EDGE,"E25.0"),sQuery(id+"F5.wireOp",EDGE,"E25.1"),sQuery(id+"F5.wireOp",EDGE,"E26.0"),sQuery(id+"F5.wireOp",EDGE,"E26.1"),sQuery(id+"F5.wireOp",EDGE,"E35.bottom"),sQuery(id+"F5.wireOp",EDGE,"E35.top"),sQuery(id+"F5.wireOp",EDGE,"E35.left"),sQuery(id+"F5.wireOp",EDGE,"E35.right"),sQuery(id+"F5.wireOp",EDGE,"E36"),sQuery(id+"F5.wireOp",EDGE,"E37"),sQuery(id+"F5.wireOp",EDGE,"E38"),sQuery(id+"F5.wireOp",EDGE,"E39"),sQuery(id+"F5.wireOp",EDGE,"E40.filletArc"),sQuery(id+"F5.wireOp",EDGE,"E41.filletArc"),sQuery(id+"F5.wireOp",EDGE,"E42.filletArc"),sQuery(id+"F5.wireOp",EDGE,"E43.filletArc"),sQuery(id+"F5.wireOp",EDGE,"E44.filletArc"),sQuery(id+"F5.wireOp",EDGE,"E45.filletArc"),sQuery(id+"F5.wireOp",EDGE,"E46.filletArc"),sQuery(id+"F5.wireOp",EDGE,"E47.filletArc"),sQuery(id+"F5.wireOp",EDGE,"E50"),sQuery(id+"F5.wireOp",EDGE,"E51"),sQuery(id+"F5.wireOp",EDGE,"E52"),sQuery(id+"F5.wireOp",EDGE,"E53"),sQuery(id+"F5.wireOp",EDGE,"E54"),sQuery(id+"F5.wireOp",EDGE,"E55"),sQuery(id+"F5.wireOp",EDGE,"E56"),sQuery(id+"F5.wireOp",EDGE,"E57")])],"isStart":false});
            extrude(context, id + "F15", {"entities" : qUnion([Q0, Q1, Q2, Q3]), "endBound" : BoundingType.UP_TO_SURFACE, "oppositeDirection" : true, "depth" : 25 * mm, "endBoundEntityFace" : qUnion([Q4]), "offsetDistance" : 25 * mm, "hasSecondDirection" : true, "secondDirectionBound" : SecondDirectionBoundingType.UP_TO_SURFACE, "secondDirectionOppositeDirection" : false, "secondDirectionDepth" : 25 * mm, "secondDirectionBoundEntityFace" : qUnion([Q5])});
        }
        {
            var Q0;
            Q0=makeQuery(id+"F11.imprint","IMPRINT",FACE,{"disambiguationData":[TD([[makeQuery(id+"F11.imprint","IMPRINT",EDGE,{"derivedFrom":sQuery(id+"F11.wireOp",EDGE,"E87.0.0")}),-1.0]])]});
            var Q1;
            Q1=makeQuery(id+"F11.imprint","IMPRINT",FACE,{"disambiguationData":[TD([[makeQuery(id+"F11.imprint","IMPRINT",EDGE,{"derivedFrom":sQuery(id+"F11.wireOp",EDGE,"E87.0.4")}),1.0]])]});
            var Q2;
            Q2=makeQuery(id+"F11.imprint","IMPRINT",FACE,{"disambiguationData":[TD([[makeQuery(id+"F11.imprint","IMPRINT",EDGE,{"derivedFrom":sQuery(id+"F11.wireOp",EDGE,"E87.0.12")}),1.0]])]});
            var Q3;
            Q3=makeQuery(id+"F7.opExtrude","CAP_FACE",FACE,{"disambiguationData":[OSD([sQuery(id+"F5.wireOp",EDGE,"E25.0"),sQuery(id+"F5.wireOp",EDGE,"E25.1"),sQuery(id+"F5.wireOp",EDGE,"E26.0"),sQuery(id+"F5.wireOp",EDGE,"E26.1"),sQuery(id+"F5.wireOp",EDGE,"E35.bottom"),sQuery(id+"F5.wireOp",EDGE,"E35.top"),sQuery(id+"F5.wireOp",EDGE,"E35.left"),sQuery(id+"F5.wireOp",EDGE,"E35.right"),sQuery(id+"F5.wireOp",EDGE,"E36"),sQuery(id+"F5.wireOp",EDGE,"E37"),sQuery(id+"F5.wireOp",EDGE,"E38"),sQuery(id+"F5.wireOp",EDGE,"E39"),sQuery(id+"F5.wireOp",EDGE,"E40.filletArc"),sQuery(id+"F5.wireOp",EDGE,"E41.filletArc"),sQuery(id+"F5.wireOp",EDGE,"E42.filletArc"),sQuery(id+"F5.wireOp",EDGE,"E43.filletArc"),sQuery(id+"F5.wireOp",EDGE,"E44.filletArc"),sQuery(id+"F5.wireOp",EDGE,"E45.filletArc"),sQuery(id+"F5.wireOp",EDGE,"E46.filletArc"),sQuery(id+"F5.wireOp",EDGE,"E47.filletArc"),sQuery(id+"F5.wireOp",EDGE,"E50"),sQuery(id+"F5.wireOp",EDGE,"E51"),sQuery(id+"F5.wireOp",EDGE,"E52"),sQuery(id+"F5.wireOp",EDGE,"E53"),sQuery(id+"F5.wireOp",EDGE,"E54"),sQuery(id+"F5.wireOp",EDGE,"E55"),sQuery(id+"F5.wireOp",EDGE,"E56"),sQuery(id+"F5.wireOp",EDGE,"E57")])],"isStart":true});
            extrude(context, id + "F16", {"entities" : qUnion([Q0, Q1, Q2]), "endBound" : BoundingType.UP_TO_SURFACE, "depth" : 25 * mm, "endBoundEntityFace" : qUnion([Q3]), "offsetDistance" : 25 * mm});
        }
        {
            var Q0;
            Q0=makeQuery(id+"F16.opExtrude","SWEPT_FACE",FACE,{"disambiguationData":[OSD([sQuery(id+"F11.wireOp",EDGE,"E96")])]});
            var sketch = newSketch(context, id + "F17", { "sketchPlane" : qUnion([Q0])});
            skLineSegment(sketch, "E97", {"start": v(263.54, 890) * mm, "end": v(263.54, 944) * mm, "construction": true});
            skCircle(sketch, "E98", {"center": v(262.5, 917) * mm, "radius": 4 * mm});
            skPoint(sketch, "E98.centerSnap0", {"position": v(263.54, 917) * mm});
            skLineSegment(sketch, "E99.0.0", {"start": v(-290, 890) * mm, "end": v(-240, 890) * mm});
            skLineSegment(sketch, "E99.0.1", {"start": v(-240, 890) * mm, "end": v(-240, 944) * mm});
            skLineSegment(sketch, "E99.0.2", {"start": v(-240, 944) * mm, "end": v(-290, 944) * mm});
            skLineSegment(sketch, "E99.0.3", {"start": v(-290, 944) * mm, "end": v(-290, 890) * mm});
            skLineSegment(sketch, "E100", {"start": v(-265, 944) * mm, "end": v(-265, 890) * mm, "construction": true});
            skCircle(sketch, "E101", {"center": v(-262.5, 917) * mm, "radius": 4 * mm});
            skPoint(sketch, "E101.centerSnap0", {"position": v(-265, 917) * mm});
            skSolve(sketch);
        }
        {
            var Q0;
            Q0=makeQuery(id+"F17.imprint","IMPRINT",FACE,{"disambiguationData":[TD([[makeQuery(id+"F17.imprint","IMPRINT",EDGE,{"derivedFrom":sQuery(id+"F17.wireOp",EDGE,"E98")}),1.0]])]});
            var Q1;
            Q1=makeQuery(id+"F17.imprint","IMPRINT",FACE,{"disambiguationData":[TD([[makeQuery(id+"F17.imprint","IMPRINT",EDGE,{"derivedFrom":sQuery(id+"F17.wireOp",EDGE,"E101")}),1.0]])]});
            var Q2;
            Q2=makeQuery(id+"F16.opExtrude","SWEPT_FACE",FACE,{"disambiguationData":[OSD([sQuery(id+"F11.wireOp",EDGE,"E90")])]});
            extrude(context, id + "F18", {"entities" : qUnion([Q0, Q1]), "endBound" : BoundingType.UP_TO_SURFACE, "depth" : 25 * mm, "endBoundEntityFace" : qUnion([Q2]), "offsetDistance" : 25 * mm});
        }
        {
            var Q0;
            Q0=makeQuery(id+"F11.imprint","IMPRINT",FACE,{"disambiguationData":[TD([[makeQuery(id+"F11.imprint","IMPRINT",EDGE,{"derivedFrom":sQuery(id+"F11.wireOp",EDGE,"E78.bottom")}),1.0]])]});
            var sketch = newSketch(context, id + "F19", { "sketchPlane" : qUnion([Q0])});
            skLineSegment(sketch, "E102.0.0", {"start": v(290, 244) * mm, "end": v(-290, 244) * mm});
            skArc(sketch, "E102.0.1", {"start": v(-290, 244) * mm, "mid": v(-293.54, 242.54) * mm, "end": v(-295, 239) * mm});
            skLineSegment(sketch, "E102.0.2", {"start": v(-295, 239) * mm, "end": v(-295, -239) * mm});
            skArc(sketch, "E102.0.3", {"start": v(-295, -239) * mm, "mid": v(-293.54, -242.54) * mm, "end": v(-290, -244) * mm});
            skLineSegment(sketch, "E102.0.4", {"start": v(-290, -244) * mm, "end": v(-240, -244) * mm});
            skArc(sketch, "E102.0.5", {"start": v(-240, -244) * mm, "mid": v(-236.46, -242.54) * mm, "end": v(-235, -239) * mm});
            skLineSegment(sketch, "E102.0.6", {"start": v(-235, -239) * mm, "end": v(-235, 179) * mm});
            skArc(sketch, "E102.0.7", {"start": v(-235, 179) * mm, "mid": v(-233.54, 182.54) * mm, "end": v(-230, 184) * mm});
            skLineSegment(sketch, "E102.0.8", {"start": v(-230, 184) * mm, "end": v(230, 184) * mm});
            skArc(sketch, "E102.0.9", {"start": v(230, 184) * mm, "mid": v(233.54, 182.54) * mm, "end": v(235, 179) * mm});
            skLineSegment(sketch, "E102.0.10", {"start": v(235, 179) * mm, "end": v(235, -239) * mm});
            skArc(sketch, "E102.0.11", {"start": v(235, -239) * mm, "mid": v(236.46, -242.54) * mm, "end": v(240, -244) * mm});
            skLineSegment(sketch, "E102.0.12", {"start": v(240, -244) * mm, "end": v(290, -244) * mm});
            skArc(sketch, "E102.0.13", {"start": v(290, -244) * mm, "mid": v(293.54, -242.54) * mm, "end": v(295, -239) * mm});
            skLineSegment(sketch, "E102.0.14", {"start": v(295, -239) * mm, "end": v(295, 239) * mm});
            skArc(sketch, "E102.0.15", {"start": v(295, 239) * mm, "mid": v(293.54, 242.54) * mm, "end": v(290, 244) * mm});
            skLineSegment(sketch, "E103", {"start": v(-295, 137.37) * mm, "end": v(295, 137.37) * mm});
            skLineSegment(sketch, "E104", {"start": v(295, 80.97) * mm, "end": v(-295, 80.97) * mm});
            skSolve(sketch);
        }
        {
            var Q0;
            {var subQ0=sQuery(id+"F19.wireOp",EDGE,"E103");var subQ1=sQuery(id+"F19.wireOp",EDGE,"E102.0.2");var subQ2=makeQuery(id+"F19.imprint","INTERSECT",VERTEX,{"derivedFrom":[subQ1,subQ0]});Q0=makeQuery(id+"F19.imprint","IMPRINT",FACE,{"disambiguationData":[TD([[makeQuery(id+"F19.imprint","IMPRINT",EDGE,{"disambiguationData":[TD([[subQ2,-1.0]])],"derivedFrom":subQ1}),1.0]])]});}
            var Q1;
            {var subQ0=sQuery(id+"F19.wireOp",EDGE,"E104");var subQ1=sQuery(id+"F19.wireOp",EDGE,"E102.0.6");var subQ2=makeQuery(id+"F19.imprint","INTERSECT",VERTEX,{"derivedFrom":[subQ1,subQ0]});Q1=makeQuery(id+"F19.imprint","IMPRINT",FACE,{"disambiguationData":[TD([[makeQuery(id+"F19.imprint","IMPRINT",EDGE,{"disambiguationData":[TD([[subQ2,-1.0]])],"derivedFrom":subQ1}),-1.0]])]});}
            var Q2;
            {var subQ0=sQuery(id+"F19.wireOp",EDGE,"E104");var subQ1=sQuery(id+"F19.wireOp",EDGE,"E102.0.10");var subQ2=makeQuery(id+"F19.imprint","INTERSECT",VERTEX,{"derivedFrom":[subQ1,subQ0]});Q2=makeQuery(id+"F19.imprint","IMPRINT",FACE,{"disambiguationData":[TD([[makeQuery(id+"F19.imprint","IMPRINT",EDGE,{"disambiguationData":[TD([[subQ2,1.0]])],"derivedFrom":subQ1}),1.0]])]});}
            extrude(context, id + "F20", {"entities" : qUnion([Q0, Q1, Q2]), "depth" : 7 * mm, "offsetDistance" : 25 * mm, "hasSecondDirection" : true, "secondDirectionOppositeDirection" : false, "secondDirectionDepth" : 1 * mm});
        }
        {
            var Q0;
            Q0=makeQuery(id+"F20.opExtrude","CAP_FACE",FACE,{"disambiguationData":[OSD([sQuery(id+"F19.wireOp",EDGE,"E102.0.2"),sQuery(id+"F19.wireOp",EDGE,"E102.0.14"),sQuery(id+"F19.wireOp",EDGE,"E103"),sQuery(id+"F19.wireOp",EDGE,"E104")])],"isStart":false});
            var Q1;
            Q1=makeQuery(id+"F7.opExtrude","CAP_FACE",FACE,{"disambiguationData":[OSD([sQuery(id+"F5.wireOp",EDGE,"E25.0"),sQuery(id+"F5.wireOp",EDGE,"E25.1"),sQuery(id+"F5.wireOp",EDGE,"E26.0"),sQuery(id+"F5.wireOp",EDGE,"E26.1"),sQuery(id+"F5.wireOp",EDGE,"E35.bottom"),sQuery(id+"F5.wireOp",EDGE,"E35.top"),sQuery(id+"F5.wireOp",EDGE,"E35.left"),sQuery(id+"F5.wireOp",EDGE,"E35.right"),sQuery(id+"F5.wireOp",EDGE,"E36"),sQuery(id+"F5.wireOp",EDGE,"E37"),sQuery(id+"F5.wireOp",EDGE,"E38"),sQuery(id+"F5.wireOp",EDGE,"E39"),sQuery(id+"F5.wireOp",EDGE,"E40.filletArc"),sQuery(id+"F5.wireOp",EDGE,"E41.filletArc"),sQuery(id+"F5.wireOp",EDGE,"E42.filletArc"),sQuery(id+"F5.wireOp",EDGE,"E43.filletArc"),sQuery(id+"F5.wireOp",EDGE,"E44.filletArc"),sQuery(id+"F5.wireOp",EDGE,"E45.filletArc"),sQuery(id+"F5.wireOp",EDGE,"E46.filletArc"),sQuery(id+"F5.wireOp",EDGE,"E47.filletArc"),sQuery(id+"F5.wireOp",EDGE,"E50"),sQuery(id+"F5.wireOp",EDGE,"E51"),sQuery(id+"F5.wireOp",EDGE,"E52"),sQuery(id+"F5.wireOp",EDGE,"E53"),sQuery(id+"F5.wireOp",EDGE,"E54"),sQuery(id+"F5.wireOp",EDGE,"E55"),sQuery(id+"F5.wireOp",EDGE,"E56"),sQuery(id+"F5.wireOp",EDGE,"E57")])],"isStart":true});
            var Q2;
            Q2=makeQuery(id+"F9.opExtrude","CAP_FACE",FACE,{"disambiguationData":[OSD([sQuery(id+"F5.wireOp",EDGE,"E55"),sQuery(id+"F5.wireOp",EDGE,"E77")])],"isStart":true});
            extrude(context, id + "F21", {"entities" : qUnion([Q0]), "endBound" : BoundingType.UP_TO_SURFACE, "depth" : 25 * mm, "endBoundEntityFace" : qUnion([Q1]), "hasOffset" : true, "offsetDistance" : 1 * mm, "hasSecondDirection" : true, "secondDirectionBound" : SecondDirectionBoundingType.UP_TO_SURFACE, "secondDirectionOppositeDirection" : false, "secondDirectionDepth" : 25 * mm, "secondDirectionBoundEntityFace" : qUnion([Q2])});
        }
        {
            var Q0;
            Q0=makeQuery(id+"F20.opExtrude","CAP_FACE",FACE,{"disambiguationData":[OSD([sQuery(id+"F19.wireOp",EDGE,"E102.0.2"),sQuery(id+"F19.wireOp",EDGE,"E102.0.14"),sQuery(id+"F19.wireOp",EDGE,"E103"),sQuery(id+"F19.wireOp",EDGE,"E104")])],"isStart":false});
            var sketch = newSketch(context, id + "F22", { "sketchPlane" : qUnion([Q0])});
            skLineSegment(sketch, "E105", {"start": v(-289, 80.97) * mm, "end": v(-289, 137.37) * mm});
            skLineSegment(sketch, "E106", {"start": v(289, 80.97) * mm, "end": v(289, 137.37) * mm});
            skSolve(sketch);
        }
        {
            var Q0;
            Q0 = qSketchRegion(id + "F22", true);
            var Q1;
            {var subQ0=sQuery(id+"F22.wireOp",EDGE,"E106");Q1=makeQuery(id+"F22.imprint","IMPRINT",FACE,{"disambiguationData":[TD([[makeQuery(id+"F22.imprint","IMPRINT",EDGE,{"derivedFrom":subQ0}),-1.0]])]});}
            var Q2;
            {var subQ0=sQuery(id+"F22.wireOp",EDGE,"E105");Q2=makeQuery(id+"F22.imprint","IMPRINT",FACE,{"disambiguationData":[TD([[makeQuery(id+"F22.imprint","IMPRINT",EDGE,{"derivedFrom":subQ0}),1.0]])]});}
            var Q3;
            Q3=makeQuery(id+"F21.opExtrude","CAP_FACE",FACE,{"disambiguationData":[OSD([sQuery(id+"F19.wireOp",EDGE,"E102.0.2"),sQuery(id+"F19.wireOp",EDGE,"E102.0.14"),sQuery(id+"F19.wireOp",EDGE,"E103"),sQuery(id+"F19.wireOp",EDGE,"E104")])],"isStart":true});
            extrude(context, id + "F23", {"entities" : qUnion([Q0, Q1, Q2]), "endBound" : BoundingType.UP_TO_SURFACE, "depth" : 25 * mm, "endBoundEntityFace" : qUnion([Q3]), "offsetDistance" : 25 * mm});
        }
    });
